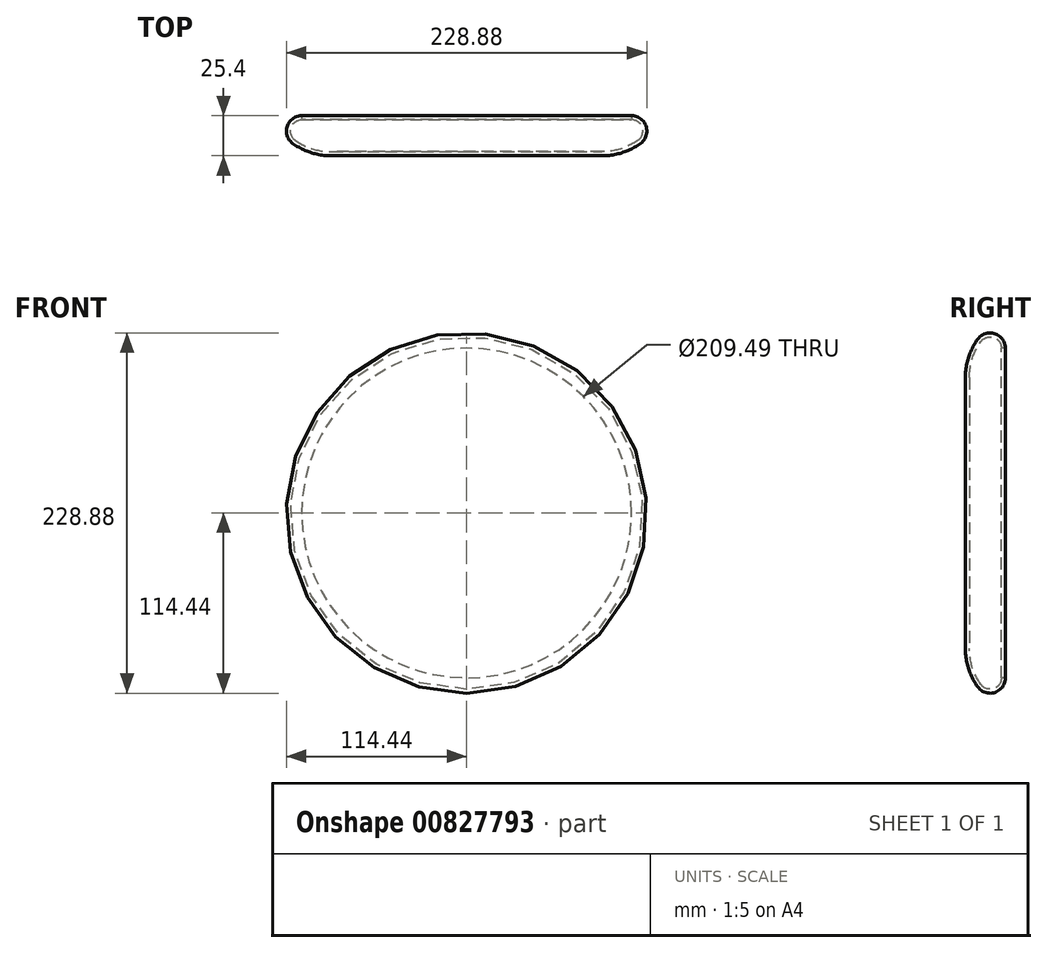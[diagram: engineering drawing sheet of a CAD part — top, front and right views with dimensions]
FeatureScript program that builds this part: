
annotation { "Feature Type Name" : "Feature", "Feature Type Description" : "" }
export const myFeature = defineFeature(function(context is Context, id is Id, definition is map)
    precondition{}
    {
        {
            var Q0;
            Q0=qCreatedBy(makeId("Front.planeOp"),FACE);
            var sketch = newSketch(context, id + "F0", { "sketchPlane" : qUnion([Q0])});
            skCircle(sketch, "E0", {"center": v(0, 0) * mm, "radius": 80.64 * mm});
            skSolve(sketch);
        }
        {
            var Q0;
            Q0=qCreatedBy(makeId("Front.planeOp"),FACE);
            var sketch = newSketch(context, id + "F1", { "sketchPlane" : qUnion([Q0])});
            skCircle(sketch, "E1", {"center": v(0, 0) * mm, "radius": 96.15 * mm});
            skSolve(sketch);
        }
        {
            var Q0;
            Q0=qCreatedBy(makeId("Front.planeOp"),FACE);
            var sketch = newSketch(context, id + "F2", { "sketchPlane" : qUnion([Q0])});
            skCircle(sketch, "E2", {"center": v(0, 0) * mm, "radius": 124.46 * mm});
            skSolve(sketch);
        }
        {
            var Q0;
            Q0=makeQuery(id+"F2.imprint","IMPRINT",FACE,{"disambiguationData":[TD([[makeQuery(id+"F2.imprint","IMPRINT",EDGE,{"derivedFrom":sQuery(id+"F2.wireOp",EDGE,"E2")}),1.0]])]});
            extrude(context, id + "F3", {"entities" : qUnion([Q0]), "depth" : 25.4 * mm, "offsetDistance" : 25.4 * mm});
        }
        {
            var Q0;
            Q0=makeQuery(id+"F3.opExtrude","CAP_EDGE",EDGE,{"disambiguationData":[OSD([sQuery(id+"F2.wireOp",EDGE,"E2")])],"isStart":false});
            fillet(context, id + "F4", {"entities" : qUnion([Q0]), "radius" : 41.7 * mm, "tangentPropagation" : true, "allowEdgeOverflow" : false});
        }
        {
            var Q0;
            {var subQ0=sQuery(id+"F2.wireOp",EDGE,"E2");Q0=makeQuery(id+"F4.opFillet","BLEND_EDGE",EDGE,{"blendedFrom":[makeQuery(id+"F3.opExtrude","CAP_EDGE",EDGE,{"disambiguationData":[OSD([subQ0])],"isStart":false}),makeQuery(id+"F3.opExtrude","CAP_FACE",FACE,{"disambiguationData":[OSD([subQ0])],"isStart":true})],"blendedInto":[makeQuery(id+"F3.opExtrude","CAP_FACE",FACE,{"disambiguationData":[OSD([subQ0])],"isStart":true})]});}
            fillet(context, id + "F5", {"entities" : qUnion([Q0]), "radius" : 9.7 * mm, "tangentPropagation" : true, "allowEdgeOverflow" : false});
        }
        {
            var Q0;
            Q0=makeQuery(id+"F3.opExtrude","CAP_FACE",FACE,{"disambiguationData":[OSD([sQuery(id+"F2.wireOp",EDGE,"E2")])],"isStart":true});
            shell(context, id + "F6", {"entities" : qUnion([Q0]), "thickness" : 2.54 * mm});
        }
    });
